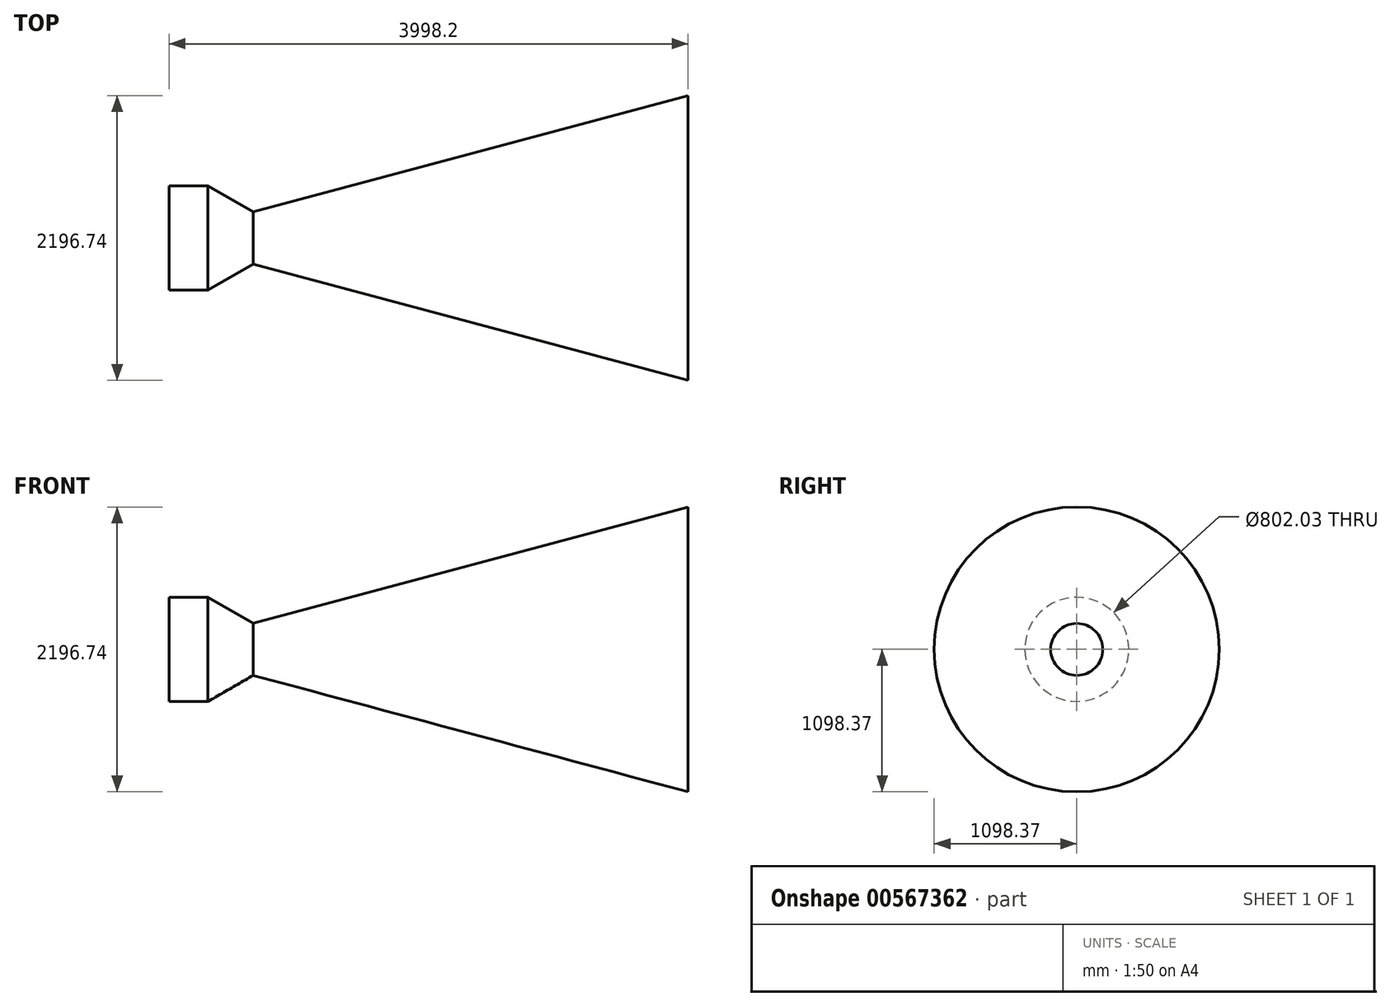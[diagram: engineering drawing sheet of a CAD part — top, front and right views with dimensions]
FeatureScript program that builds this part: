
annotation { "Feature Type Name" : "Feature", "Feature Type Description" : "" }
export const myFeature = defineFeature(function(context is Context, id is Id, definition is map)
    precondition{}
    {
        {
            var Q0;
            Q0=qCreatedBy(makeId("Front.planeOp"),FACE);
            var sketch = newSketch(context, id + "F0", { "sketchPlane" : qUnion([Q0])});
            skLineSegment(sketch, "E0", {"start": v(-647.3, 401.01) * mm, "end": v(-347.3, 401.01) * mm});
            skLineSegment(sketch, "E1", {"start": v(-347.3, 401.01) * mm, "end": v(0, 200.5) * mm});
            skLineSegment(sketch, "E2", {"start": v(0, 200.5) * mm, "end": v(3350.9, 1098.37) * mm});
            skSolve(sketch);
        }
        {
            var Q0;
            Q0=qCreatedBy(makeId("Top.planeOp"),FACE);
            var sketch = newSketch(context, id + "F1", { "sketchPlane" : qUnion([Q0])});
            skLineSegment(sketch, "E3", {"start": v(0, 0) * mm, "end": v(75.38, 0) * mm});
            skSolve(sketch);
        }
        {
            var Q0;
            Q0 = qConstructionFilter(qBodyType(qCreatedBy(id + "F0" ,EDGE), BodyType.WIRE), ConstructionObject.NO);
            var Q1;
            Q1=sQuery(id+"F1.wireOp",EDGE,"E3");
            revolve(context, id + "F2", {"bodyType" : ToolBodyType.SURFACE, "surfaceEntities" : qUnion([Q0]), "axis" : qUnion([Q1]), "revolveType" : RevolveType.FULL});
        }
    });
